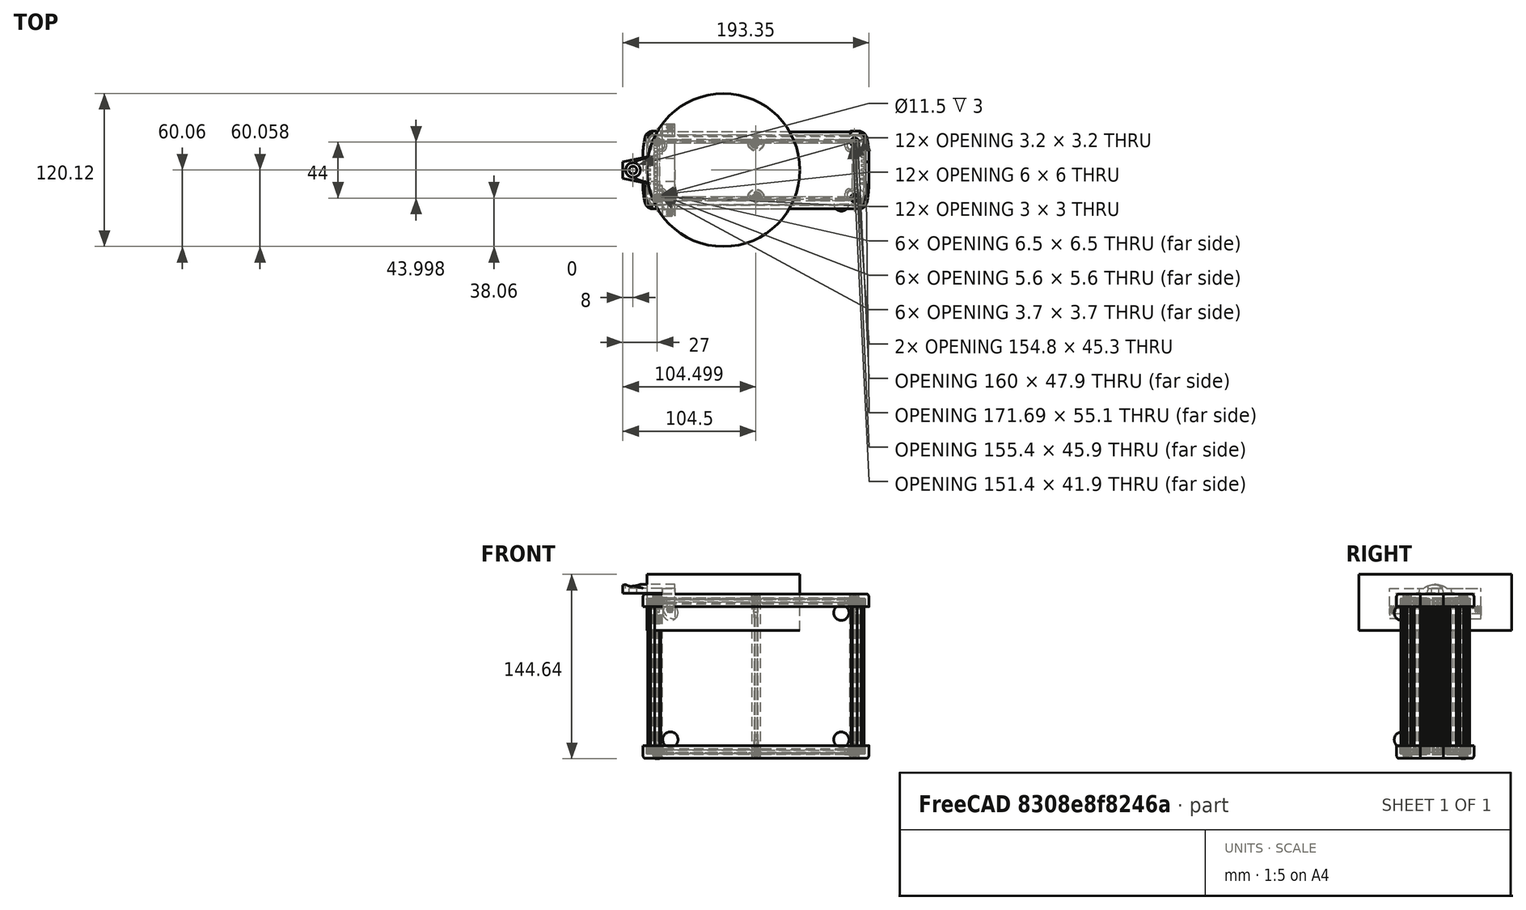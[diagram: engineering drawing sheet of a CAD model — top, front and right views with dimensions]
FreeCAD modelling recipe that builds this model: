
FCSTD DOCUMENT  (FreeCAD 0.20R29177 (Git))
Label: antennaHolder2022_07_19
License: All rights reserved
LicenseURL: http://en.wikipedia.org/wiki/All_rights_reserved
objects: Part::Cylinder×8, Part::MultiFuse×5, Part::Box×4, Part::Feature×3, Part::Cut×3, Part::Cone×1, Part::MultiCommon×1
note: 25 computed .brp shape members not serialized (recipe doc carries the construction recipe); baked Part::Feature solids carry a one-line shape summary decoded from their .brp

FEATURE [Part::Feature] Feature  label="EX-64-002"
  Placement = pos=(73.5,0,0) rot=(0,0,1;0rad)
  shape: bbox 178.8 x 63.35 x 129.6 mm, 1628 faces, 33 solids (baked)
FEATURE [Part::Box] Box  label="out"
  AttacherType = Attacher::AttachEngine3D
  Height = 24
  Length = 10
  Placement = pos=(0,-36,45) rot=(0,0,1;0rad)
  Width = 72
FEATURE [Part::Box] Box001  label="in"
  AttacherType = Attacher::AttachEngine3D
  Height = 11
  Length = 10
  Placement = pos=(0,-31,54) rot=(0,0,1;0rad)
  Width = 62
FEATURE [Part::Box] Box002  label="in001"
  AttacherType = Attacher::AttachEngine3D
  Height = 11
  Length = 10
  Placement = pos=(0,-27,45) rot=(0,0,1;0rad)
  Width = 54
FEATURE [Part::MultiFuse] Fusion  label="in002"
  Shapes = -> [Box001,Box002]
FEATURE [Part::Cut] Cut
  Base = -> Box
  Tool = -> Fusion
FEATURE [Part::Feature] Solid  label="m3HeatSetInsert"
  Placement = pos=(6,31.5,52.5) rot=(0,0,1;0rad)
  shape: bbox 4.772 x 4.354 x 4.772 mm, 239 faces (baked)
FEATURE [Part::Cylinder] Cylinder
  Angle = 90
  AttacherType = Attacher::AttachEngine3D
  FirstAngle = 0
  Height = 5
  Placement = pos=(10,31,55) rot=(0.57735,-0.57735,-0.57735;4.18879rad)
  Radius = 10
  SecondAngle = 0
FEATURE [Part::Feature] Solid001  label="m3HeatSetInsert001"
  Placement = pos=(6,-31,52.5) rot=(0,0,1;3.14159rad)
  shape: bbox 4.772 x 4.354 x 4.772 mm, 239 faces (baked)
FEATURE [Part::Cylinder] Cylinder001
  Angle = 90
  AttacherType = Attacher::AttachEngine3D
  FirstAngle = 0
  Height = 5
  Placement = pos=(10,-31,55) rot=(0,0.707107,-0.707107;3.14159rad)
  Radius = 10
  SecondAngle = 0
FEATURE [Part::MultiFuse] Fusion001  label="out001"
  Shapes = -> [Cylinder,Cylinder001,Cut]
FEATURE [Part::Cylinder] Cylinder014  label="antennaIn001"
  Angle = 360
  AttacherType = Attacher::AttachEngine3D
  FirstAngle = 0
  Height = 10
  Placement = pos=(-23,0,69) rot=(0,0,1;0rad)
  Radius = 5.75
  SecondAngle = 0
FEATURE [Part::Cylinder] Cylinder013  label="antennaIn"
  Angle = 360
  AttacherType = Attacher::AttachEngine3D
  FirstAngle = 0
  Height = 10
  Placement = pos=(-23,0,65) rot=(0,0,1;0rad)
  Radius = 3
  SecondAngle = 0
FEATURE [Part::MultiFuse] Fusion003
  Shapes = -> [Cylinder013,Cylinder014]
FEATURE [Part::Cylinder] Cylinder016  label="m3HeastSetCut"
  Angle = 360
  AttacherType = Attacher::AttachEngine3D
  FirstAngle = 0
  Height = 94
  Placement = pos=(6,-47.35,51) rot=(-1,0,0;1.5708rad)
  Radius = 2
  SecondAngle = 0
FEATURE [Part::Cylinder] Cylinder017  label="include001"
  Angle = 90
  AttacherType = Attacher::AttachEngine3D
  FirstAngle = 0
  Height = 87
  Placement = pos=(10,-40.75,55) rot=(0.57735,-0.57735,-0.57735;4.18879rad)
  Radius = 10
  SecondAngle = 0
FEATURE [Part::Box] Box004  label="include"
  AttacherType = Attacher::AttachEngine3D
  Height = 14
  Length = 42
  Placement = pos=(-31,-36,55) rot=(0,0,1;0rad)
  Width = 82
FEATURE [Part::Cylinder] Cylinder018
  Angle = 360
  AttacherType = Attacher::AttachEngine3D
  FirstAngle = 0
  Height = 42
  Placement = pos=(-31,0,57) rot=(0.57735,0.57735,0.57735;2.0944rad)
  Radius = 15
  SecondAngle = 0
FEATURE [Part::Cylinder] Cylinder019
  Angle = 360
  AttacherType = Attacher::AttachEngine3D
  FirstAngle = 0
  Height = 44
  Placement = pos=(48,0,35.9) rot=(0,0,1;0rad)
  Radius = 60.06
  SecondAngle = 0
FEATURE [Part::Cone] Cone
  Angle = 180
  AttacherType = Attacher::AttachEngine3D
  Height = 41
  Placement = pos=(10,-1.8e-15,65) rot=(-0.57735,0.57735,0.57735;4.18879rad)
  Radius1 = 15
  Radius2 = 6.5
FEATURE [Part::MultiFuse] Fusion004
  Shapes = -> [Fusion001,Cone]
FEATURE [Part::Cut] Cut001
  Base = -> Fusion004
  Tool = -> Cylinder016
FEATURE [Part::Cut] Cut002
  Base = -> Cut001
  Tool = -> Fusion003
FEATURE [Part::MultiFuse] Fusion005  label="include002"
  Shapes = -> [Cylinder018,Box004,Cylinder017]
FEATURE [Part::MultiCommon] Common
  Shapes = -> [Cut002,Fusion005]
